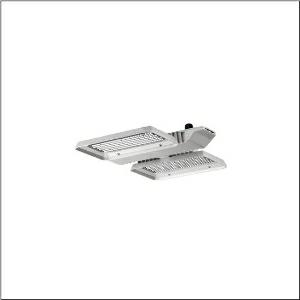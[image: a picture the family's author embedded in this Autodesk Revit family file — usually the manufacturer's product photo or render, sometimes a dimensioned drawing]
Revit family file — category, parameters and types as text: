
# Revit family: highbay_21_51hla2d14fcb
name_source: partatom
category: Lighting Fixtures
units: mm (PartAtom-declared; Revit-internal decimal feet)

## family parameters
Cut with Voids When Loaded = No
Host = Face
Light Source = No
Part Type = Normal
Room Calculation Point = No
Round Connector Dimension = Use Diameter
Shared = No

## types (1)
- --- (1 x LED, 13800 lm, 85.5 W, 4000K)
    Apparent Load = 86 VA
    CIE Flux Codes = 89 96 99 100 100
    Color Rendering = 80
    Color Temperature = 4000K
    Default Elevation = 1800 mm
    Description = Highbay 21, LED high bay luminaire, primary light control with lens, of PMMA, light emission: direct distribution, primary light characteristic: symmetric, installation type: suspended mounting, surface-mounted, for 1x 2 x LED rated luminous flux: 13.800 lm, light colour: 840, colour temperature: 4000K, control gear: ECG DALI, with terminal, 5-pole, max. 2.5mm², mains connection: 230..240V, AC, 50/60Hz, rated input power: 86W, LED unit, of diecast aluminium, unplated, bead blasted, silver, length: 470 mm, width: 500 mm, height: 65mm, housing, of diecast aluminium, uncoated, bead blasted, silver, protection rating (complete): IP65, insulation class (complete): insulation class I (protective earthing), certification: CE, ENEC, VDE, protection symbol: D, impact resistance: IK08 with glass or PC cover, permissible ambient temperature for indoor applications: -35..+45°C, corresponds to IFS (International Featured Standards) requirements for safety and quality in the food industry, reducing of maximum allowable ambient temperature of 5°C with ceiling mounting, packaging unit: 1 piece
    Height = 95 mm
    Lamp = 1 x LED
    Lamp Light Flux = 13800 lm
    Lamp Power = 85.5 W
    Lamp count = 1
    Length = 468 mm
    Luminous efficacy = 161 lm/W
    Manufacturer = Siteco
    ModVariant = No
    Model = 51HLA2D14FCB
    Mounting Place = Ceiling
    Mounting Type = Pendant
    Number of Poles = 1
    OnlyDefault = Yes
    Power Factor = 1
    Product Name = Highbay 21
    Product group = LED high bay luminaire
    ProductGroupID = 903
    Protection Class = Protection class I
    Protection Degree = IP 65
    RLX_Detail_Level = 1
    RlxData = <blob elided: 53277 chars, md5=3e436cb9>
    Socket = socket
    Standby Power = 0 W
    System Light Flux = 13800 lm
    System Power = 86 W
    Type Comments = factory setting: luminous flux: 100 % | dim-lin: 254 | 491 mA
    Type Image = l_1003425.jpg
    URL = http://relux.com
    VarID = @adj_135771
    Voltage = 0 V
    Weight = 0.00 kg
    Width = 501 mm

## geometry (parser evidence)
native form markers: Blend x4, Sweep x16
no freeform markers — native parametric forms only
